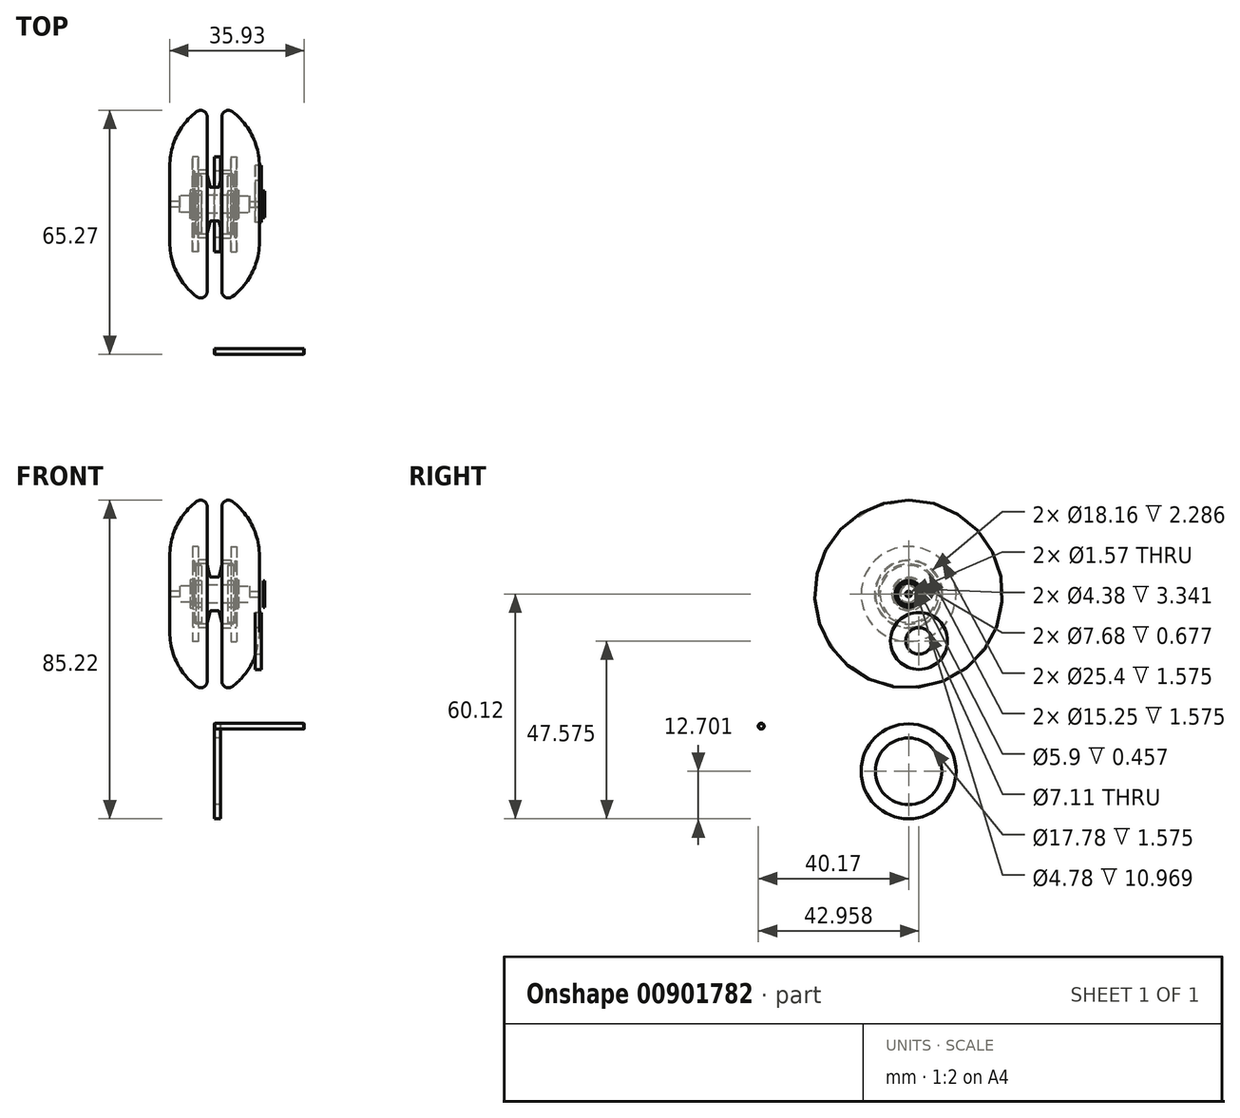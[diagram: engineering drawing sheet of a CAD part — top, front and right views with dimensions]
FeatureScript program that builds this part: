
annotation { "Feature Type Name" : "Feature", "Feature Type Description" : "" }
export const myFeature = defineFeature(function(context is Context, id is Id, definition is map)
    precondition{}
    {
        {
            var Q0;
            Q0=qCreatedBy(makeId("Top.planeOp"),FACE);
            var sketch = newSketch(context, id + "F0", { "sketchPlane" : qUnion([Q0])});
            skLineSegment(sketch, "E0", {"start": v(-43.15, 0) * mm, "end": v(47.7, 0) * mm, "construction": true});
            skLineSegment(sketch, "E1", {"start": v(0, 35.7) * mm, "end": v(0, -27.9) * mm, "construction": true});
            skLineSegment(sketch, "E2", {"start": v(-1.98, 7.95) * mm, "end": v(-1.25, 4.77) * mm});
            skLineSegment(sketch, "E3", {"start": v(-0.9, 4.49) * mm, "end": v(0.9, 4.49) * mm});
            skLineSegment(sketch, "E4", {"start": v(1.25, 4.77) * mm, "end": v(1.98, 7.95) * mm});
            skPoint(sketch, "E5.visualSharp", {"position": v(-1.19, 4.49) * mm});
            skArc(sketch, "E5.filletArc", {"start": v(-1.25, 4.77) * mm, "mid": v(-1.12, 4.57) * mm, "end": v(-0.9, 4.49) * mm});
            skPoint(sketch, "E6.visualSharp", {"position": v(1.19, 4.49) * mm});
            skArc(sketch, "E6.filletArc", {"start": v(0.9, 4.49) * mm, "mid": v(1.12, 4.57) * mm, "end": v(1.25, 4.77) * mm});
            skLineSegment(sketch, "E7", {"start": v(-2.1, 8.05) * mm, "end": v(-4.9, 8.05) * mm});
            skLineSegment(sketch, "E8.MirrorCS", {"start": v(2.1, 8.05) * mm, "end": v(4.9, 8.05) * mm});
            skLineSegment(sketch, "E9.MirrorCS", {"start": v(5.02, 7.92) * mm, "end": v(5.02, 7.62) * mm});
            skPoint(sketch, "E10.visualSharp", {"position": v(-5.02, 8.05) * mm});
            skArc(sketch, "E10.filletArc", {"start": v(-4.9, 8.05) * mm, "mid": v(-4.99, 8.01) * mm, "end": v(-5.02, 7.92) * mm});
            skPoint(sketch, "E11.visualSharp", {"position": v(-2, 8.05) * mm});
            skArc(sketch, "E11.filletArc", {"start": v(-1.98, 7.95) * mm, "mid": v(-2.02, 8.02) * mm, "end": v(-2.1, 8.05) * mm});
            skPoint(sketch, "E12.visualSharp", {"position": v(2, 8.05) * mm});
            skArc(sketch, "E12.filletArc", {"start": v(2.1, 8.05) * mm, "mid": v(2.02, 8.02) * mm, "end": v(1.98, 7.95) * mm});
            skPoint(sketch, "E13.visualSharp", {"position": v(5.02, 8.05) * mm});
            skArc(sketch, "E13.filletArc", {"start": v(5.02, 7.92) * mm, "mid": v(4.99, 8.01) * mm, "end": v(4.9, 8.05) * mm});
            skLineSegment(sketch, "E14", {"start": v(-5.02, 7.92) * mm, "end": v(-5.02, 7.62) * mm});
            skLineSegment(sketch, "E15", {"start": v(-5.02, 7.62) * mm, "end": v(-3.45, 7.62) * mm});
            skLineSegment(sketch, "E16", {"start": v(-3.45, 7.62) * mm, "end": v(-3.45, 3.55) * mm});
            skLineSegment(sketch, "E17", {"start": v(-3.45, 3.55) * mm, "end": v(-5.02, 3.55) * mm});
            skLineSegment(sketch, "E18.MirrorCS", {"start": v(5.02, 7.62) * mm, "end": v(3.45, 7.62) * mm});
            skLineSegment(sketch, "E19.MirrorCS", {"start": v(3.45, 7.62) * mm, "end": v(3.45, 3.55) * mm});
            skLineSegment(sketch, "E20.MirrorCS", {"start": v(3.45, 3.55) * mm, "end": v(5.02, 3.55) * mm});
            skLineSegment(sketch, "E21", {"start": v(-5.48, 2.39) * mm, "end": v(-5.48, 2.95) * mm});
            skLineSegment(sketch, "E22", {"start": v(-5.48, 2.95) * mm, "end": v(-5.02, 2.95) * mm});
            skLineSegment(sketch, "E23", {"start": v(-5.02, 3.55) * mm, "end": v(-5.02, 2.95) * mm});
            skLineSegment(sketch, "E24.MirrorCS", {"start": v(5.02, 3.55) * mm, "end": v(5.02, 2.95) * mm});
            skLineSegment(sketch, "E25.MirrorCS", {"start": v(5.48, 2.95) * mm, "end": v(5.02, 2.95) * mm});
            skLineSegment(sketch, "E26.MirrorCS", {"start": v(5.48, 2.39) * mm, "end": v(5.48, 2.95) * mm});
            skLineSegment(sketch, "E27", {"start": v(-5.48, 2.39) * mm, "end": v(5.48, 2.39) * mm});
            skSolve(sketch);
        }
        {
            var Q0;
            Q0=qCreatedBy(makeId("Right.planeOp"),FACE);
            var sketch = newSketch(context, id + "F1", { "sketchPlane" : qUnion([Q0])});
            skCircle(sketch, "E28", {"center": v(-39.39, -35.37) * mm, "radius": 0.79 * mm});
            skSolve(sketch);
        }
        {
            var Q0;
            Q0 = qSketchRegion(id + "F1", true);
            extrude(context, id + "F2", {"entities" : qUnion([Q0]), "depth" : 23.95 * mm, "offsetDistance" : 25.4 * mm});
        }
        {
            var Q0;
            Q0=makeQuery(id+"F2.opExtrude","CAP_EDGE",EDGE,{"disambiguationData":[OSD([sQuery(id+"F1.wireOp",EDGE,"E28")])],"isStart":false});
            var Q1;
            Q1=makeQuery(id+"F2.opExtrude","CAP_EDGE",EDGE,{"disambiguationData":[OSD([sQuery(id+"F1.wireOp",EDGE,"E28")])],"isStart":true});
            chamfer(context, id + "F3", {"entities" : qUnion([Q0, Q1]), "width" : 0.09 * mm, "tangentPropagation" : true});
        }
        {
            var Q0;
            Q0=qCreatedBy(makeId("Top.planeOp"),FACE);
            var sketch = newSketch(context, id + "F4", { "sketchPlane" : qUnion([Q0])});
            skLineSegment(sketch, "E29", {"start": v(-48.04, 0) * mm, "end": v(12.58, 0) * mm, "construction": true});
            skLineSegment(sketch, "E30", {"start": v(-11.98, 10.2) * mm, "end": v(-11.98, 0.79) * mm});
            skLineSegment(sketch, "E31", {"start": v(-11.98, 0.79) * mm, "end": v(-9.37, 0.79) * mm});
            skLineSegment(sketch, "E32", {"start": v(-9.37, 0.79) * mm, "end": v(-9.37, 2.2) * mm});
            skPoint(sketch, "E33.visualSharp", {"position": v(-1.51, 24.87) * mm});
            skArc(sketch, "E33.filletArc", {"start": v(-1.95, 23.32) * mm, "mid": v(-2.94, 24.91) * mm, "end": v(-4.81, 24.73) * mm});
            skArc(sketch, "E34", {"start": v(-4.81, 24.73) * mm, "mid": v(-10.09, 18.3) * mm, "end": v(-11.98, 10.2) * mm});
            skLineSegment(sketch, "E35", {"start": v(-1.95, 23.32) * mm, "end": v(-1.95, 9.2) * mm});
            skLineSegment(sketch, "E36", {"start": v(-2.08, 9.08) * mm, "end": v(-2.65, 9.08) * mm});
            skLineSegment(sketch, "E37", {"start": v(-6.49, 3.84) * mm, "end": v(-6.49, 2.95) * mm});
            skLineSegment(sketch, "E38", {"start": v(-6.49, 2.95) * mm, "end": v(-6.03, 2.95) * mm});
            skLineSegment(sketch, "E39", {"start": v(-6.03, 2.95) * mm, "end": v(-6.03, 2.2) * mm});
            skLineSegment(sketch, "E40", {"start": v(-5.43, 3.84) * mm, "end": v(-5.43, 8.9) * mm});
            skLineSegment(sketch, "E41", {"start": v(-5.43, 8.9) * mm, "end": v(-5.94, 8.9) * mm});
            skLineSegment(sketch, "E42", {"start": v(-5.94, 8.9) * mm, "end": v(-5.94, 12.7) * mm});
            skLineSegment(sketch, "E43", {"start": v(-5.94, 12.7) * mm, "end": v(-4.36, 12.7) * mm});
            skLineSegment(sketch, "E44", {"start": v(-4.36, 9.2) * mm, "end": v(-4.36, 12.7) * mm});
            skLineSegment(sketch, "E45", {"start": v(-4.26, 9.08) * mm, "end": v(-2.65, 9.08) * mm});
            skPoint(sketch, "E46.visualSharp", {"position": v(-1.95, 9.08) * mm});
            skArc(sketch, "E46.filletArc", {"start": v(-2.08, 9.08) * mm, "mid": v(-1.99, 9.12) * mm, "end": v(-1.95, 9.2) * mm});
            skPoint(sketch, "E47.visualSharp", {"position": v(-4.36, 9.08) * mm});
            skLineSegment(sketch, "E48", {"start": v(-6.49, 3.84) * mm, "end": v(-5.43, 3.84) * mm});
            skLineSegment(sketch, "E49", {"start": v(-4.36, 9.2) * mm, "end": v(-4.36, 9.08) * mm});
            skLineSegment(sketch, "E50", {"start": v(-4.26, 9.08) * mm, "end": v(-4.36, 9.08) * mm});
            skLineSegment(sketch, "E51", {"start": v(-9.37, 2.2) * mm, "end": v(-6.03, 2.2) * mm});
            skSolve(sketch);
        }
        {
            var Q0;
            Q0=makeQuery(id+"F4.imprint","IMPRINT",FACE,{"disambiguationData":[TD([[makeQuery(id+"F4.imprint","IMPRINT",EDGE,{"derivedFrom":sQuery(id+"F4.wireOp",EDGE,"E30")}),1.0]])]});
            var Q1;
            Q1=sQuery(id+"F4.wireOp",EDGE,"E29");
            revolve(context, id + "F5", {"surfaceOperationType" : NewSurfaceOperationType.NEW, "entities" : qUnion([Q0]), "axis" : qUnion([Q1]), "revolveType" : RevolveType.FULL});
        }
        {
            var Q0;
            Q0 = qSketchRegion(id + "F0", true);
            var Q1;
            Q1=sQuery(id+"F0.wireOp",EDGE,"E0");
            revolve(context, id + "F6", {"surfaceOperationType" : NewSurfaceOperationType.NEW, "entities" : qUnion([Q0]), "axis" : qUnion([Q1]), "revolveType" : RevolveType.FULL});
        }
        {
            var Q0;
            Q0=makeQuery(id+"F5.opRevolve","SWEPT_BODY",BODY,{"disambiguationData":[OSD([sQuery(id+"F4.wireOp",EDGE,"E30"),sQuery(id+"F4.wireOp",EDGE,"E31"),sQuery(id+"F4.wireOp",EDGE,"E32"),sQuery(id+"F4.wireOp",EDGE,"E33.filletArc"),sQuery(id+"F4.wireOp",EDGE,"E34"),sQuery(id+"F4.wireOp",EDGE,"E35"),sQuery(id+"F4.wireOp",EDGE,"E36"),sQuery(id+"F4.wireOp",EDGE,"da237736-d7f9-4b6c-b57e-93ea38959bfb"),sQuery(id+"F4.wireOp",EDGE,"E37"),sQuery(id+"F4.wireOp",EDGE,"E38"),sQuery(id+"F4.wireOp",EDGE,"E39"),sQuery(id+"F4.wireOp",EDGE,"KE9W3pVK-VeS7-iO4B-E9TI-OXFRdq51j9FU"),sQuery(id+"F4.wireOp",EDGE,"E40"),sQuery(id+"F4.wireOp",EDGE,"E41"),sQuery(id+"F4.wireOp",EDGE,"E42"),sQuery(id+"F4.wireOp",EDGE,"E43"),sQuery(id+"F4.wireOp",EDGE,"E44"),sQuery(id+"F4.wireOp",EDGE,"E45"),sQuery(id+"F4.wireOp",EDGE,"E46.filletArc"),sQuery(id+"F4.wireOp",EDGE,"E47.filletArc"),sQuery(id+"F4.wireOp",EDGE,"E48")])]});
            var Q1;
            Q1=qCreatedBy(makeId("Right.planeOp"),FACE);
            mirror(context, id + "F7", {"entities" : qUnion([Q0]), "mirrorPlane" : qUnion([Q1])});
        }
        {
            var Q0;
            Q0=makeQuery(id+"F6.opRevolve","SWEPT_FACE",FACE,{"disambiguationData":[OSD([sQuery(id+"F0.wireOp",EDGE,"E19.MirrorCS")])]});
            var sketch = newSketch(context, id + "F8", { "sketchPlane" : qUnion([Q0])});
            skCircle(sketch, "E52.0", {"center": v(2.79, -34.82) * mm, "radius": 7.62 * mm});
            skCircle(sketch, "E53.0", {"center": v(2.79, -34.82) * mm, "radius": 3.55 * mm});
            skSolve(sketch);
        }
        {
            var Q0;
            Q0=makeQuery(id+"F8.imprint","IMPRINT",FACE,{"disambiguationData":[TD([[makeQuery(id+"F8.imprint","IMPRINT",EDGE,{"derivedFrom":sQuery(id+"F8.wireOp",EDGE,"E52.0")}),1.0]])]});
            extrude(context, id + "F9", {"entities" : qUnion([Q0]), "depth" : 1.57 * mm, "offsetDistance" : 25.4 * mm});
        }
        {
            var Q0;
            Q0=makeQuery(id+"F9.opExtrude","SWEPT_BODY",BODY,{"disambiguationData":[OSD([sQuery(id+"F0.wireOp",EDGE,"E18.MirrorCS"),sQuery(id+"F0.wireOp",EDGE,"E19.MirrorCS"),sQuery(id+"F0.wireOp",EDGE,"E20.MirrorCS"),sQuery(id+"F8.wireOp",EDGE,"E52.0")])]});
            var Q1;
            Q1=sQuery(id+"F4.wireOp",EDGE,"E29");
            transform(context, id + "F10", {"entities" : qUnion([Q0]), "transformType" : TransformType.TRANSLATION_3D, "dx" : 7.44 * mm, "dy" : 0 * mm, "dz" : 0 * mm, "makeCopy" : false});
        }
        {
            var Q0;
            Q0=makeQuery(id+"F6.opRevolve","SWEPT_FACE",FACE,{"disambiguationData":[OSD([sQuery(id+"F0.wireOp",EDGE,"E24.MirrorCS")])]});
            var sketch = newSketch(context, id + "F11", { "sketchPlane" : qUnion([Q0])});
            skCircle(sketch, "E54.0", {"center": v(0, 0) * mm, "radius": 2.95 * mm});
            skCircle(sketch, "E55.0", {"center": v(0, 0) * mm, "radius": 3.55 * mm});
            skSolve(sketch);
        }
        {
            var Q0;
            Q0=makeQuery(id+"F11.imprint","IMPRINT",FACE,{"disambiguationData":[TD([[makeQuery(id+"F11.imprint","IMPRINT",EDGE,{"derivedFrom":sQuery(id+"F11.wireOp",EDGE,"E54.0")}),1.0]])]});
            extrude(context, id + "F12", {"entities" : qUnion([Q0]), "depth" : 0.46 * mm, "offsetDistance" : 25.4 * mm});
        }
        {
            var Q0;
            Q0=makeQuery(id+"F12.opExtrude","SWEPT_BODY",BODY,{"disambiguationData":[OSD([sQuery(id+"F11.wireOp",EDGE,"E54.0"),sQuery(id+"F11.wireOp",EDGE,"E55.0")])]});
            transform(context, id + "F13", {"entities" : qUnion([Q0]), "transformType" : TransformType.TRANSLATION_3D, "dx" : 7.95 * mm, "dy" : 0 * mm, "dz" : 0 * mm, "makeCopy" : false});
        }
        {
            var Q0;
            Q0=makeQuery(id+"F9.opExtrude","SWEPT_BODY",BODY,{"disambiguationData":[OSD([sQuery(id+"F8.wireOp",EDGE,"E52.0"),sQuery(id+"F8.wireOp",EDGE,"E53.0")])]});
            transform(context, id + "F14", {"entities" : qUnion([Q0]), "transformType" : TransformType.TRANSLATION_3D, "dx" : 0 * mm, "dy" : 0 * mm, "dz" : 22.28 * mm, "makeCopy" : false});
        }
        {
            var Q0;
            Q0=qCreatedBy(makeId("Right.planeOp"),FACE);
            var sketch = newSketch(context, id + "F15", { "sketchPlane" : qUnion([Q0])});
            skCircle(sketch, "E56", {"center": v(0, -47.42) * mm, "radius": 8.9 * mm});
            skCircle(sketch, "E57", {"center": v(0, -47.42) * mm, "radius": 12.7 * mm});
            skSolve(sketch);
        }
        {
            var Q0;
            Q0=makeQuery(id+"F15.imprint","IMPRINT",FACE,{"disambiguationData":[TD([[makeQuery(id+"F15.imprint","IMPRINT",EDGE,{"derivedFrom":sQuery(id+"F15.wireOp",EDGE,"E56")}),-1.0]])]});
            extrude(context, id + "F16", {"entities" : qUnion([Q0]), "depth" : 1.57 * mm, "offsetDistance" : 25.4 * mm});
        }
        {
            var Q0;
            Q0=makeQuery(id+"F5.opRevolve","SWEPT_EDGE",EDGE,{"disambiguationData":[OSD([sQuery(id+"F4.wireOp",EDGE,"E40"),sQuery(id+"F4.wireOp",EDGE,"E48")])]});
            chamfer(context, id + "F17", {"entities" : qUnion([Q0]), "width" : 0.38 * mm, "tangentPropagation" : true});
        }
        {
            var Q0;
            Q0=makeQuery(id+"F7.opPattern","COPY",EDGE,{"derivedFrom":makeQuery(id+"F5.opRevolve","SWEPT_EDGE",EDGE,{"disambiguationData":[OSD([sQuery(id+"F4.wireOp",EDGE,"E40"),sQuery(id+"F4.wireOp",EDGE,"E48")])]}),"instanceName":"1"});
            chamfer(context, id + "F18", {"entities" : qUnion([Q0]), "width" : 0.38 * mm, "tangentPropagation" : true});
        }
    });
